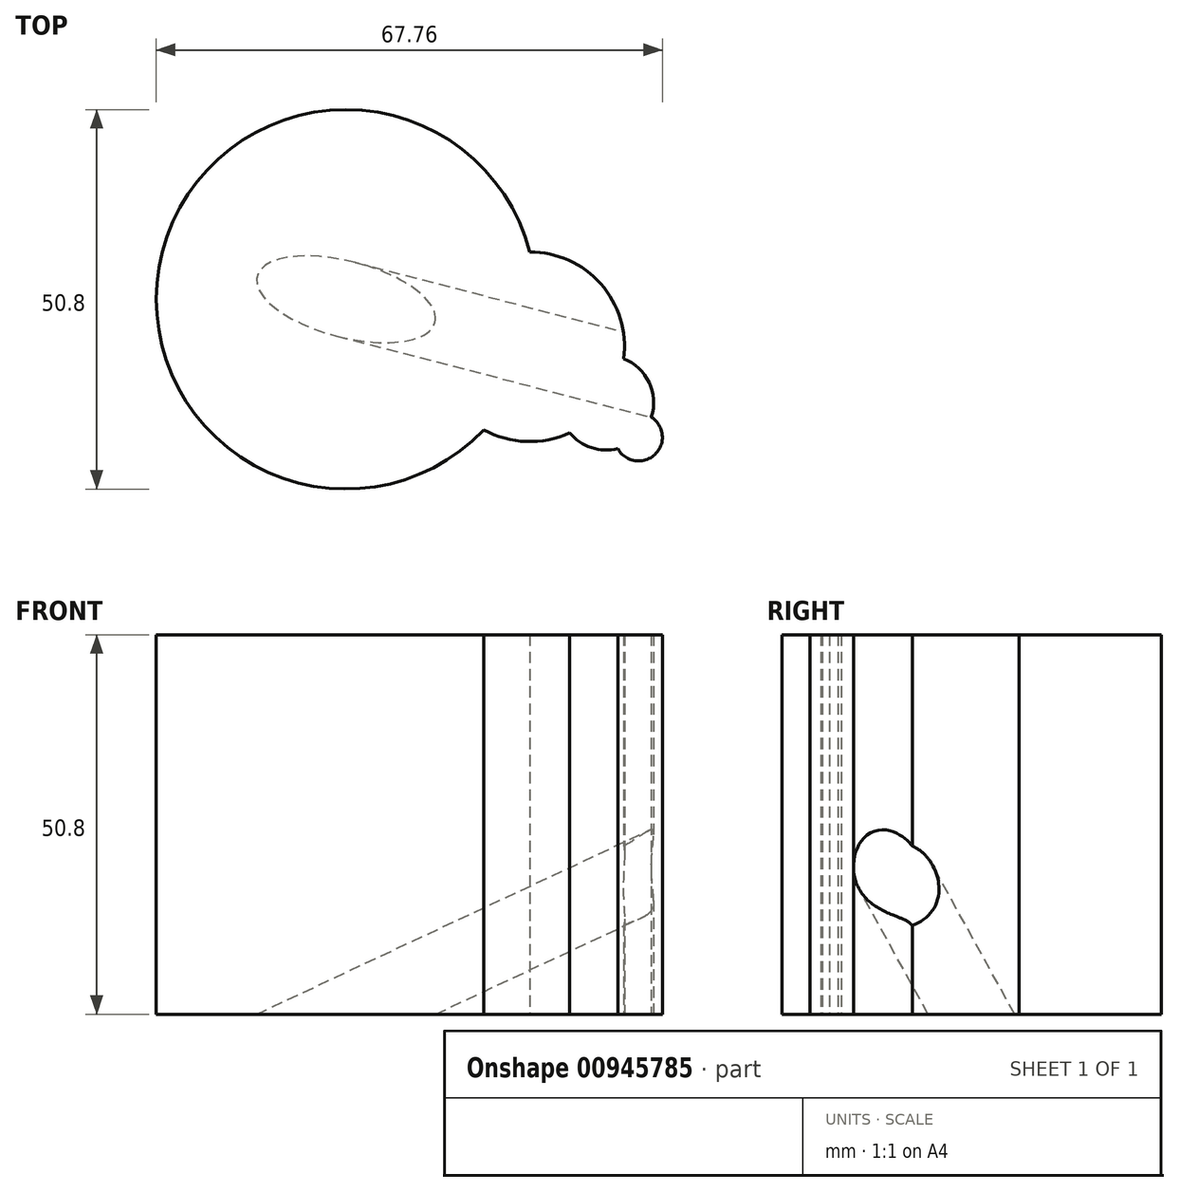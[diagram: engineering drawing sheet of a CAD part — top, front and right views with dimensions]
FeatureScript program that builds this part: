
annotation { "Feature Type Name" : "Feature", "Feature Type Description" : "" }
export const myFeature = defineFeature(function(context is Context, id is Id, definition is map)
    precondition{}
    {
        {
            var Q0;
            Q0=qCreatedBy(makeId("Top.planeOp"),FACE);
            var sketch = newSketch(context, id + "F0", { "sketchPlane" : qUnion([Q0])});
            skCircle(sketch, "E0", {"center": v(0, 0) * mm, "radius": 25.4 * mm});
            skCircle(sketch, "E1", {"center": v(24.6, -6.35) * mm, "radius": 12.7 * mm});
            skCircle(sketch, "E2", {"center": v(34.85, -13.84) * mm, "radius": 6.35 * mm});
            skCircle(sketch, "E3", {"center": v(39.19, -18.48) * mm, "radius": 3.18 * mm});
            skArc(sketch, "E4", {"start": v(41.13, -20.99) * mm, "mid": v(11.04, -1.21) * mm, "end": v(-24.6, -6.35) * mm});
            skSolve(sketch);
        }
        {
            var Q0;
            {var subQ0=sQuery(id+"F0.wireOp",EDGE,"E4");var subQ1=sQuery(id+"F0.wireOp",EDGE,"E0");var subQ2=makeQuery(id+"F0.imprint","INTERSECT",VERTEX,{"disambiguationData":[OD(0.0)],"derivedFrom":[subQ1,subQ0]});Q0=makeQuery(id+"F0.imprint","IMPRINT",FACE,{"disambiguationData":[TD([[makeQuery(id+"F0.imprint","IMPRINT",EDGE,{"disambiguationData":[TD([[subQ2,1.0]])],"derivedFrom":subQ1}),1.0]])]});}
            var Q1;
            {var subQ0=sQuery(id+"F0.wireOp",EDGE,"E4");var subQ1=sQuery(id+"F0.wireOp",EDGE,"E0");var subQ2=makeQuery(id+"F0.imprint","INTERSECT",VERTEX,{"disambiguationData":[OD(0.0)],"derivedFrom":[subQ1,subQ0]});Q1=makeQuery(id+"F0.imprint","IMPRINT",FACE,{"disambiguationData":[TD([[makeQuery(id+"F0.imprint","IMPRINT",EDGE,{"disambiguationData":[TD([[subQ2,-1.0]])],"derivedFrom":subQ1}),1.0]])]});}
            var Q2;
            {var subQ0=sQuery(id+"F0.wireOp",EDGE,"E1");var subQ1=sQuery(id+"F0.wireOp",EDGE,"E0");var subQ2=makeQuery(id+"F0.imprint","INTERSECT",VERTEX,{"disambiguationData":[OD(1.0)],"derivedFrom":[subQ1,subQ0]});Q2=makeQuery(id+"F0.imprint","IMPRINT",FACE,{"disambiguationData":[TD([[makeQuery(id+"F0.imprint","IMPRINT",EDGE,{"disambiguationData":[TD([[subQ2,-1.0]])],"derivedFrom":subQ1}),1.0]])]});}
            var Q3;
            {var subQ0=sQuery(id+"F0.wireOp",EDGE,"E1");var subQ1=sQuery(id+"F0.wireOp",EDGE,"E0");var subQ2=makeQuery(id+"F0.imprint","INTERSECT",VERTEX,{"disambiguationData":[OD(0.0)],"derivedFrom":[subQ1,subQ0]});Q3=makeQuery(id+"F0.imprint","IMPRINT",FACE,{"disambiguationData":[TD([[makeQuery(id+"F0.imprint","IMPRINT",EDGE,{"disambiguationData":[TD([[subQ2,1.0]])],"derivedFrom":subQ1}),1.0]])]});}
            var Q4;
            {var subQ0=sQuery(id+"F0.wireOp",EDGE,"E1");var subQ1=sQuery(id+"F0.wireOp",EDGE,"E0");var subQ2=makeQuery(id+"F0.imprint","INTERSECT",VERTEX,{"disambiguationData":[OD(0.0)],"derivedFrom":[subQ1,subQ0]});Q4=makeQuery(id+"F0.imprint","IMPRINT",FACE,{"disambiguationData":[TD([[makeQuery(id+"F0.imprint","IMPRINT",EDGE,{"disambiguationData":[TD([[subQ2,1.0]])],"derivedFrom":subQ1}),-1.0]])]});}
            var Q5;
            {var subQ0=sQuery(id+"F0.wireOp",EDGE,"E1");var subQ1=sQuery(id+"F0.wireOp",EDGE,"E0");var subQ2=makeQuery(id+"F0.imprint","INTERSECT",VERTEX,{"disambiguationData":[OD(1.0)],"derivedFrom":[subQ1,subQ0]});Q5=makeQuery(id+"F0.imprint","IMPRINT",FACE,{"disambiguationData":[TD([[makeQuery(id+"F0.imprint","IMPRINT",EDGE,{"disambiguationData":[TD([[subQ2,-1.0]])],"derivedFrom":subQ1}),-1.0]])]});}
            var Q6;
            {var subQ0=sQuery(id+"F0.wireOp",EDGE,"E2");var subQ1=sQuery(id+"F0.wireOp",EDGE,"E1");var subQ2=makeQuery(id+"F0.imprint","INTERSECT",VERTEX,{"disambiguationData":[OD(0.0)],"derivedFrom":[subQ1,subQ0]});Q6=makeQuery(id+"F0.imprint","IMPRINT",FACE,{"disambiguationData":[TD([[makeQuery(id+"F0.imprint","IMPRINT",EDGE,{"disambiguationData":[TD([[subQ2,-1.0]])],"derivedFrom":subQ1}),1.0]])]});}
            var Q7;
            {var subQ0=sQuery(id+"F0.wireOp",EDGE,"E2");var subQ1=sQuery(id+"F0.wireOp",EDGE,"E1");var subQ2=makeQuery(id+"F0.imprint","INTERSECT",VERTEX,{"disambiguationData":[OD(1.0)],"derivedFrom":[subQ1,subQ0]});Q7=makeQuery(id+"F0.imprint","IMPRINT",FACE,{"disambiguationData":[TD([[makeQuery(id+"F0.imprint","IMPRINT",EDGE,{"disambiguationData":[TD([[subQ2,1.0]])],"derivedFrom":subQ1}),1.0]])]});}
            var Q8;
            {var subQ0=sQuery(id+"F0.wireOp",EDGE,"E2");var subQ1=sQuery(id+"F0.wireOp",EDGE,"E1");var subQ2=makeQuery(id+"F0.imprint","INTERSECT",VERTEX,{"disambiguationData":[OD(1.0)],"derivedFrom":[subQ1,subQ0]});Q8=makeQuery(id+"F0.imprint","IMPRINT",FACE,{"disambiguationData":[TD([[makeQuery(id+"F0.imprint","IMPRINT",EDGE,{"disambiguationData":[TD([[subQ2,1.0]])],"derivedFrom":subQ1}),-1.0]])]});}
            var Q9;
            {var subQ0=sQuery(id+"F0.wireOp",EDGE,"E2");var subQ1=sQuery(id+"F0.wireOp",EDGE,"E1");var subQ2=makeQuery(id+"F0.imprint","INTERSECT",VERTEX,{"disambiguationData":[OD(0.0)],"derivedFrom":[subQ1,subQ0]});Q9=makeQuery(id+"F0.imprint","IMPRINT",FACE,{"disambiguationData":[TD([[makeQuery(id+"F0.imprint","IMPRINT",EDGE,{"disambiguationData":[TD([[subQ2,-1.0]])],"derivedFrom":subQ1}),-1.0]])]});}
            var Q10;
            {var subQ0=sQuery(id+"F0.wireOp",EDGE,"E3");var subQ1=sQuery(id+"F0.wireOp",EDGE,"E2");var subQ2=makeQuery(id+"F0.imprint","INTERSECT",VERTEX,{"disambiguationData":[OD(0.0)],"derivedFrom":[subQ1,subQ0]});Q10=makeQuery(id+"F0.imprint","IMPRINT",FACE,{"disambiguationData":[TD([[makeQuery(id+"F0.imprint","IMPRINT",EDGE,{"disambiguationData":[TD([[subQ2,-1.0]])],"derivedFrom":subQ1}),1.0]])]});}
            var Q11;
            {var subQ0=sQuery(id+"F0.wireOp",EDGE,"E3");var subQ1=sQuery(id+"F0.wireOp",EDGE,"E2");var subQ2=makeQuery(id+"F0.imprint","INTERSECT",VERTEX,{"disambiguationData":[OD(1.0)],"derivedFrom":[subQ1,subQ0]});Q11=makeQuery(id+"F0.imprint","IMPRINT",FACE,{"disambiguationData":[TD([[makeQuery(id+"F0.imprint","IMPRINT",EDGE,{"disambiguationData":[TD([[subQ2,1.0]])],"derivedFrom":subQ1}),1.0]])]});}
            var Q12;
            {var subQ0=sQuery(id+"F0.wireOp",EDGE,"E3");var subQ1=sQuery(id+"F0.wireOp",EDGE,"E2");var subQ2=makeQuery(id+"F0.imprint","INTERSECT",VERTEX,{"disambiguationData":[OD(1.0)],"derivedFrom":[subQ1,subQ0]});Q12=makeQuery(id+"F0.imprint","IMPRINT",FACE,{"disambiguationData":[TD([[makeQuery(id+"F0.imprint","IMPRINT",EDGE,{"disambiguationData":[TD([[subQ2,1.0]])],"derivedFrom":subQ1}),-1.0]])]});}
            var Q13;
            {var subQ0=sQuery(id+"F0.wireOp",EDGE,"E3");var subQ1=sQuery(id+"F0.wireOp",EDGE,"E2");var subQ2=makeQuery(id+"F0.imprint","INTERSECT",VERTEX,{"disambiguationData":[OD(0.0)],"derivedFrom":[subQ1,subQ0]});Q13=makeQuery(id+"F0.imprint","IMPRINT",FACE,{"disambiguationData":[TD([[makeQuery(id+"F0.imprint","IMPRINT",EDGE,{"disambiguationData":[TD([[subQ2,-1.0]])],"derivedFrom":subQ1}),-1.0]])]});}
            extrude(context, id + "F1", {"entities" : qUnion([Q0, Q1, Q2, Q3, Q4, Q5, Q6, Q7, Q8, Q9, Q10, Q11, Q12, Q13]), "depth" : 50.8 * mm, "offsetDistance" : 25.4 * mm});
        }
        {
            var Q0;
            Q0=makeQuery(id+"F1.opExtrude","CAP_EDGE",EDGE,{"disambiguationData":[OSD([sQuery(id+"F0.wireOp",EDGE,"E3")])],"isStart":true});
            cPoint(context, id + "F2", {"entities" : qUnion([Q0]), "parameter" : 0.5});
        }
        {
            var Q0;
            {var subQ0=sQuery(id+"F0.wireOp",EDGE,"E1");var subQ1=sQuery(id+"F0.wireOp",EDGE,"E0");Q0=makeQuery(id+"F1.opExtrude","CAP_VERTEX",VERTEX,{"disambiguationData":[OSD([subQ1,subQ0]),TDD([makeQuery(id+"F0.imprint","INTERSECT",VERTEX,{"disambiguationData":[OD(1.0)],"derivedFrom":[subQ1,subQ0]})])],"isStart":false});}
            var Q1;
            {var subQ0=sQuery(id+"F0.wireOp",EDGE,"E1");var subQ1=sQuery(id+"F0.wireOp",EDGE,"E0");Q1=makeQuery(id+"F1.opExtrude","CAP_VERTEX",VERTEX,{"disambiguationData":[OSD([subQ1,subQ0]),TDD([makeQuery(id+"F0.imprint","INTERSECT",VERTEX,{"disambiguationData":[OD(0.0)],"derivedFrom":[subQ1,subQ0]})])],"isStart":false});}
            var Q2;
            Q2 = qCreatedBy(id + "F2" ,VERTEX);
            cPlane(context, id + "F3", {"entities" : qUnion([Q0, Q1, Q2]), "cplaneType" : CPlaneType.THREE_POINT, "offset" : 25.4 * mm, "width" : 152.4 * mm, "height" : 152.4 * mm});
        }
        {
            var Q0;
            Q0=qCreatedBy(id+"F3.planeOp",FACE);
            var sketch = newSketch(context, id + "F4", { "sketchPlane" : qUnion([Q0])});
            skCircle(sketch, "E5", {"center": v(0, 0) * mm, "radius": 5.08 * mm});
            skSolve(sketch);
        }
        {
            var Q0;
            Q0 = qSketchRegion(id + "F4", true);
            extrude(context, id + "F5", {"entities" : qUnion([Q0]), "operationType" : NewBodyOperationType.REMOVE, "endBound" : BoundingType.SYMMETRIC, "oppositeDirection" : true, "depth" : 127 * mm, "offsetDistance" : 25.4 * mm});
        }
    });
